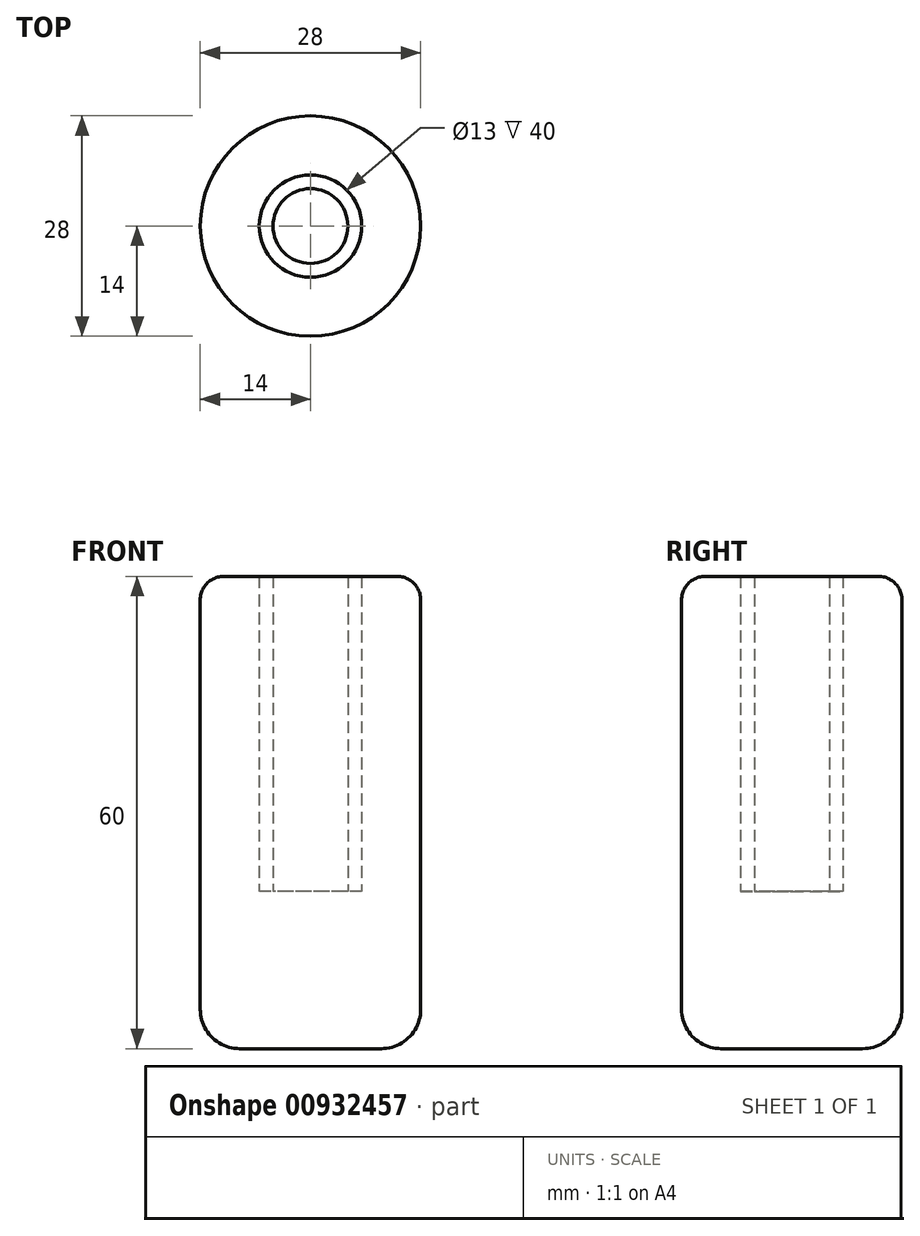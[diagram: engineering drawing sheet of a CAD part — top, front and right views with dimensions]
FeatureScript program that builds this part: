
annotation { "Feature Type Name" : "Feature", "Feature Type Description" : "" }
export const myFeature = defineFeature(function(context is Context, id is Id, definition is map)
    precondition{}
    {
        {
            var Q0;
            Q0=qCreatedBy(makeId("Top.planeOp"),FACE);
            var sketch = newSketch(context, id + "F0", { "sketchPlane" : qUnion([Q0])});
            skCircle(sketch, "E0", {"center": v(0, 0) * mm, "radius": 7.5 * mm});
            skCircle(sketch, "E1", {"center": v(0, 0) * mm, "radius": 9 * mm});
            skCircle(sketch, "E2", {"center": v(0, 0) * mm, "radius": 14 * mm});
            skSolve(sketch);
        }
        {
            var Q0;
            Q0 = qSketchRegion(id + "F0", true);
            var Q1;
            Q1=makeQuery(id+"F0.imprint","IMPRINT",FACE,{"disambiguationData":[TD([[makeQuery(id+"F0.imprint","IMPRINT",EDGE,{"derivedFrom":sQuery(id+"F0.wireOp",EDGE,"E0")}),1.0]])]});
            var Q2;
            Q2=makeQuery(id+"F0.imprint","IMPRINT",FACE,{"disambiguationData":[TD([[makeQuery(id+"F0.imprint","IMPRINT",EDGE,{"derivedFrom":sQuery(id+"F0.wireOp",EDGE,"E0")}),-1.0]])]});
            extrude(context, id + "F1", {"entities" : qUnion([Q0, Q1, Q2]), "depth" : 20 * mm, "offsetDistance" : 25 * mm});
        }
        {
            var Q0;
            Q0=makeQuery(id+"F1.opExtrude","CAP_FACE",FACE,{"disambiguationData":[OSD([sQuery(id+"F0.wireOp",EDGE,"E2")])],"isStart":false});
            var sketch = newSketch(context, id + "F2", { "sketchPlane" : qUnion([Q0])});
            skCircle(sketch, "E3", {"center": v(0, 0) * mm, "radius": 14 * mm});
            skCircle(sketch, "E4", {"center": v(0, 0) * mm, "radius": 6.5 * mm});
            skCircle(sketch, "E5", {"center": v(0, 0) * mm, "radius": 4.75 * mm});
            skSolve(sketch);
        }
        {
            var Q0;
            Q0=makeQuery(id+"F2.imprint","IMPRINT",FACE,{"disambiguationData":[TD([[makeQuery(id+"F2.imprint","IMPRINT",EDGE,{"derivedFrom":sQuery(id+"F2.wireOp",EDGE,"E5")}),1.0]])]});
            var Q1;
            Q1=makeQuery(id+"F2.imprint","IMPRINT",FACE,{"disambiguationData":[TD([[makeQuery(id+"F2.imprint","IMPRINT",EDGE,{"derivedFrom":sQuery(id+"F2.wireOp",EDGE,"E3")}),1.0]])]});
            extrude(context, id + "F3", {"entities" : qUnion([Q0, Q1]), "operationType" : NewBodyOperationType.ADD, "depth" : 40 * mm, "offsetDistance" : 25 * mm});
        }
        {
            var Q0;
            Q0=makeQuery(id+"F1.opExtrude","CAP_EDGE",EDGE,{"disambiguationData":[OSD([sQuery(id+"F0.wireOp",EDGE,"E2")])],"isStart":true});
            fillet(context, id + "F4", {"entities" : qUnion([Q0]), "radius" : 5 * mm, "tangentPropagation" : true, "allowEdgeOverflow" : false});
        }
        {
            var Q0;
            Q0=makeQuery(id+"F3.opExtrude","CAP_EDGE",EDGE,{"disambiguationData":[OSD([sQuery(id+"F2.wireOp",EDGE,"E3")])],"isStart":false});
            fillet(context, id + "F5", {"entities" : qUnion([Q0]), "radius" : 3 * mm, "tangentPropagation" : true, "allowEdgeOverflow" : false});
        }
    });
